# Revit family: TAG1
name_source: partatom
category: Furniture
units: mm (PartAtom-declared; Revit-internal decimal feet)

## family parameters
Always vertical = Yes
Cut with Voids When Loaded = No
OmniClass Number = 23.40.20.00
OmniClass Title = General Furniture and Specialties
Render Appearance Source = Family Geometry
Room Calculation Point = No
Shared = No
Work Plane-Based = No

## types (1)
- CW008
    Default Elevation = 0 mm  [stored 0 ft]
    Description = 2 x CaseWorks Backsplash Laminate 04Hx24W, 2 x CaseWorks Backsplash Laminate 04Hx60W, 2 x CaseWorks Countertop Laminate 24Dx60W, 1 x CaseWorks Toe Kick 04Hx72W (Cut to size on-site), 1 x CaseWorks Toe Kick 04Hx84W (Cut to size on-site), 2 x CaseWorks Side Toe Kick 04Hx20.22W (Cut to size on-site), 1 x CaseWorks Base Cabinet Single Door Right 35Hx18Wx24D, 1 x CaseWorks Base Cabinet Double Doors & Drawers 35Hx30Wx24D, 1 x CaseWorks Base Cabinet Four Drawers 35Hx24Wx24D, 1 x CaseWorks Base Cabinet Single Drawer w Cubby 35Hx30Wx24D, 1 x CaseWorks Base Cabinet Open 35Hx18Wx24D, 1 x CaseWorks Storage Cabinet Open 78Hx18Wx24D, 1 x CaseWorks Storage Cabinet Open 78Hx18Wx24D, 1 x 86 Degree Hinge Restriction Clip, 1 x Soft Close Mechanism for Hinged Doors, 2 x Cbx Tackboard Wall Mount 35hx60w
    Exported From CET Designer = Yes
    Manufacturer = AIS
    Model = M-ABL0424
    Show CW008 = Yes
    VisibilityIndex = 0

note: [stored X ft] marks values corroborated as IEEE doubles in the binary element streams (Revit-internal decimal feet)

## geometry (parser evidence)
native form markers: Sweep x3
no freeform markers — native parametric forms only
